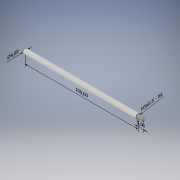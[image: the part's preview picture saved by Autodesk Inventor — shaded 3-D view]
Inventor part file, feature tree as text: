
AUTODESK INVENTOR PART (.ipt)
format: ipt  version: 2019.4 (Build 234330000, 330)  size: 113,664 bytes
history: native  units: mm
features: other x4, extrude x2, thread x2, sketch x2
ambient origin geometry x8: Origin, YZ Plane, XZ Plane, XY Plane, X Axis, Y Axis, Z Axis, Center Point
bodies: Solid1 (feature_tree)
feature tree (10):
  other  "Annotations"
  extrude  "Extrusion1"  Depth=100.0mm TaperAngle=0.0deg
  extrude  "Extrusion2"  Depth=5.0mm TaperAngle=0.0deg
  thread  "Thread1"  [1 undecoded]
  sketch  "Sketch1"  dims[d0=4.0mm d1=100.0mm d2=0.0mm]
  sketch  "Sketch2"  dims[d3=3.0mm d4=5.0mm d5=0.0mm d6=10.0mm d7=0.0mm d10=15.344009mm d11=4.0mm d12=100.0mm d13=5.0mm d8=48.811845mm d9=3.0mm]
  thread  "Thread Note 1"  [1 undecoded]
  other  "Diameter Dimension 1"
  other  "Linear Dimension 1"
  other  "Linear Dimension 2"
note: 2 required parameter values undecoded (feature->parameter linkage not recoverable at this tier; creation-order binding heuristic only, values carry confidence <= 0.55)
